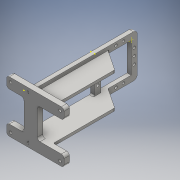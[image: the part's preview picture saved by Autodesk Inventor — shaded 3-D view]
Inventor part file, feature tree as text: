
AUTODESK INVENTOR PART (.ipt)
format: ipt  version: 2016 (Build 200138000, 138)  size: 352,256 bytes
history: native  units: mm
features: sketch x22, hole x12, fillet x12, extrude x11
ambient origin geometry x8: Origin, YZ Plane, XZ Plane, XY Plane, X Axis, Y Axis, Z Axis, Center Point
bodies: 实体1 (feature_tree)
feature tree (57):
  sketch  "草图1"  dims[d0=32.0mm d1=32.0mm]
  extrude  "拉伸1"  Depth=32.0mm
  sketch  "草图3"  dims[d4=3.0mm d5=0.0mm]
  hole  "孔1"  [1 undecoded]
  sketch  "草图4"  dims[d6=2.35mm d16=16.0mm d8=2.0mm d9=6.0mm d10=3.023mm d11=2.0mm d12=14.3117mm d13=8.0mm d14=20.594885mm]
  sketch  "草图5"  dims[d17=2.35mm d18=16.0mm d19=2.0mm d20=6.0mm d21=3.023mm d22=2.0mm d23=14.3117mm d24=8.0mm d25=20.594885mm]
  hole  "孔2"  [1 undecoded]
  hole  "孔3"  [1 undecoded]
  hole  "孔4"  [1 undecoded]
  hole  "孔5"  [1 undecoded]
  hole  "孔6"  [1 undecoded]
  hole  "孔7"  [1 undecoded]
  hole  "孔8"  [1 undecoded]
  hole  "孔9"  [1 undecoded]
  hole  "孔10"  [1 undecoded]
  hole  "孔11"  [1 undecoded]
  hole  "孔12"  [1 undecoded]
  extrude  "拉伸2"  Depth=4.0mm TaperAngle=0.0deg
  sketch  "草图7"  dims[d35=2.35mm d36=16.0mm d37=2.0mm d38=6.0mm d39=3.023mm d40=2.0mm d41=14.3117mm d42=8.0mm d43=20.594885mm]
  sketch  "草图8"  dims[d44=5.9mm d45=2.35mm d46=2.0mm d47=6.0mm d48=3.023mm d49=2.0mm d50=14.3117mm d51=8.0mm d52=20.594885mm]
  sketch  "草图9"  dims[d53=2.35mm d64=10.0mm d55=2.0mm d56=6.0mm d57=3.023mm d58=2.0mm d59=14.3117mm d60=8.0mm d61=20.594885mm]
  sketch  "草图10"  dims[d62=5.9mm d63=2.35mm d65=2.0mm d66=6.0mm d67=3.023mm d68=2.0mm d69=14.3117mm d70=8.0mm d71=20.594885mm d72=5.9mm d73=2.35mm]
  sketch  "草图11"  dims[d74=2.0mm d75=6.0mm d76=3.023mm d77=2.0mm d78=14.3117mm d79=8.0mm d80=20.594885mm d81=5.9mm d82=2.35mm]
  sketch  "草图12"  dims[d83=2.0mm d84=6.0mm d85=3.023mm d86=2.0mm d87=14.3117mm d88=8.0mm d89=20.594885mm d90=5.9mm d91=2.35mm]
  extrude  "拉伸3"  Depth=3.0mm
  extrude  "拉伸4"  Depth=3.0mm TaperAngle=0.0deg
  extrude  "拉伸5"  Depth=4.0mm
  extrude  "拉伸6"  Depth=3.0mm
  fillet  "圆角1"  Radius=4.0mm
  fillet  "圆角2"  Radius=3.0mm
  extrude  "拉伸7"  Depth=2.0mm
  extrude  "拉伸8"  Depth=2.0mm
  fillet  "圆角3"  Radius=3.0mm
  fillet  "圆角4"  Radius=1.0mm
  fillet  "圆角5"  Radius=1.0mm
  fillet  "圆角6"  Radius=1.0mm
  fillet  "圆角7"  Radius=1.0mm
  fillet  "圆角8"  Radius=1.0mm
  fillet  "圆角9"  Radius=1.0mm
  fillet  "圆角10"  Radius=1.0mm
  sketch  "草图17"  dims[d124=10.0mm d125=15.0mm]
  sketch  "草图18"  dims[d126=2.0mm d127=0.0mm d128=2.0mm d129=0.0mm]
  sketch  "草图19"  dims[d130=50.0mm d131=0.0mm d146=2.0mm]
  extrude  "拉伸9"  Depth=1.0mm
  extrude  "拉伸10"  Depth=2.0mm
  extrude  "拉伸11"  Depth=2.0mm
  fillet  "圆角11"  Radius=2.0mm
  fillet  "圆角12"  Radius=2.0mm
  sketch  "草图2"  dims[d2=22.7mm d3=22.7mm]
  sketch  "草图6"  dims[d26=2.35mm d27=16.0mm d28=2.0mm d29=6.0mm d30=3.023mm d31=2.0mm d32=14.3117mm d33=8.0mm d34=20.594885mm]
  sketch  "草图13"  dims[d92=2.0mm d93=6.0mm d94=3.023mm d95=2.0mm d96=14.3117mm d97=8.0mm d98=20.594885mm d99=5.9mm d100=2.35mm]
  sketch  "草图14"  dims[d101=2.0mm d102=6.0mm d103=3.023mm d104=2.0mm d105=14.3117mm d106=8.0mm d107=20.594885mm d108=5.9mm d109=2.35mm]
  sketch  "草图15"  dims[d110=2.0mm d111=6.0mm d112=3.023mm d113=2.0mm d114=14.3117mm d115=8.0mm d116=20.594885mm d117=2.0mm d118=0.0mm]
  sketch  "草图16"  dims[d121=15.0mm d123=10.0mm]
  sketch  "草图20"  dims[d149=2.0mm d152=2.0mm]
  sketch  "草图21"  dims[d154=2.0mm d155=4.0mm d156=0.0mm]
  sketch  "草图22"  dims[d157=3.0mm d158=3.0mm d159=3.0mm d160=0.0mm d161=4.0mm d163=3.0mm d166=4.0mm d167=3.0mm d168=2.0mm d169=2.0mm d170=3.0mm d171=0.0mm d172=1.0mm d173=1.0mm d174=1.0mm d175=1.0mm d176=1.0mm d177=1.0mm d178=1.0mm d179=1.0mm d183=2.0mm d186=2.0mm d187=2.0mm d188=2.0mm d189=4.0mm d190=0.0mm d191=3.0mm d192=0.0mm d193=3.0mm d194=0.0mm d195=2.0mm d196=2.0mm d7=1.0mm]
note: 12 required parameter values undecoded (feature->parameter linkage not recoverable at this tier; creation-order binding heuristic only, values carry confidence <= 0.55)
